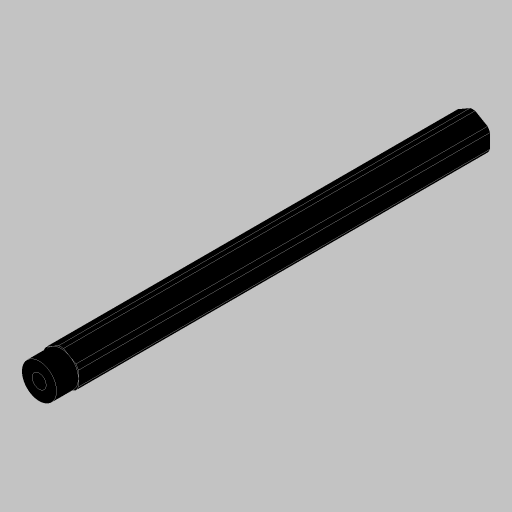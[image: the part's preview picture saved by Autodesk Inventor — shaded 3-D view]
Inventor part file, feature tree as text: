
AUTODESK INVENTOR PART (.ipt)
format: ipt  version: 2023.5 (Build 275446000, 446)  size: 145,920 bytes
history: native  units: in
note: dims shown in document units (in); Inventor stores cm internally (conversion verified against a paired STEP export)
features: extrude x3, projected_geometry x3, hole x1, sketch x1
ambient origin geometry x8: Origin, YZ Plane, XZ Plane, XY Plane, X Axis, Y Axis, Z Axis, Center Point
bodies: Solid1 (feature_tree)
feature tree (8):
  extrude  "Extrusion1"  Depth=0.315in
  hole  "Hole1"  [1 undecoded]
  extrude  "Extrusion3"  Depth=0.5in
  extrude  "Extrusion4"  Depth=0.315in TaperAngle=0.0deg
  sketch  "Sketch5"  dims[d2=0.0in d9=0.625in d10=0.385in d11=0.25in d12=0.5635in d13=1.0in d14=0.8108in d16=0.7in d17=0.0in d18=0.0in d19=0.5in d20=0.315in d21=0.0in]
  projected_geometry  "Projected Loop2"
  projected_geometry  "Project Cut Edges1"
  projected_geometry  "Project Cut Edges2"
note: 1 required parameter value undecoded (feature->parameter linkage not recoverable at this tier; creation-order binding heuristic only, values carry confidence <= 0.55)
